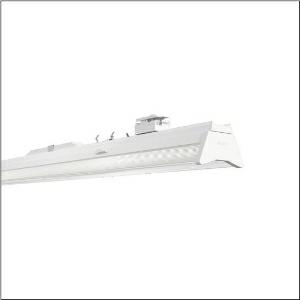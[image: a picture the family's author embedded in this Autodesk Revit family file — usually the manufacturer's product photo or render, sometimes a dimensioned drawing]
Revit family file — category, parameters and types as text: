
# Revit family: licross_11_performance_mo_51tm16mn4axg
name_source: partatom
category: Lighting Fixtures
units: mm (PartAtom-declared; Revit-internal decimal feet)

## family parameters
Cut with Voids When Loaded = No
Host = Face
Light Source = No
Part Type = Normal
Room Calculation Point = No
Round Connector Dimension = Use Diameter
Shared = No

## types (1)
- --- (1 x LED, 10160 lm, 55.3 W, 4000K)
    Apparent Load = 55 VA
    CIE Flux Codes = 66 88 96 79 100
    Color Rendering = 80
    Color Temperature = 4000K
    Default Elevation = 1800 mm
    Description = Licross 11 Performance MO, luminaire insert, of sheet steel, galvanised, coil coated, white, length: 1.500mm, width: 120mm, height: 123mm, LED rated luminous flux: 10.160lm, light colour: 840, SDCM (Standard Deviation of Colour Matching)MacAdam ≤ 2 SDCM (initial), control gear: ON/OFF Multilumen, with plug, 3-pole, with phase selection, mains connection: 220..240V, AC, 50/60Hz, rated input power: 55W, internal wiring halogen-free, primary light control with lens, of plastic, primary optical cover: cover, of PMMA, light emission: direct/indirect distribution, primary light characteristic: symmetric, protection rating (complete): IP40, insulation class (complete): insulation class I (protective earthing), certification: CE, ENEC, VDE, UKCA, protection symbol: D if used in an environment without relevant dust loads with corresponding accessories, impact resistance: IK06, permissible ambient temperature for indoor applications: -35..+40°C, corresponds to IFS (International Featured Standards) requirements for safety and quality in the food industry, reducing of maximum allowable ambient temperature of 5°C with ceiling mounting, LABS conformity tested according to VDMA 24364:2018-05, The light source and the operating device comply with the requirements of the Ecodesign Regulation (EU) 2019/2020 and are replaceable in accordance with this regulation, packaging unit: 1 piece
    Height = 114 mm
    Lamp = 1 x LED
    Lamp Light Flux = 10160 lm
    Lamp Power = 55.3 W
    Lamp count = 1
    Length = 1500 mm
    Luminous efficacy = 184 lm/W
    Manufacturer = Siteco
    ModVariant = No
    Model = 51TM16MN4AXG
    Mounting Place = Ceiling
    Mounting Type = Pendant
    Number of Poles = 1
    OnlyDefault = Yes
    Power Factor = 1
    Product Name = Licross 11 Performance MO
    Product group = luminaire insert | ceiling pendant
    ProductGroupID = 901
    Protection Class = Protection class I
    Protection Degree = IP 40
    RLX_Detail_Level = 1
    RLX_Emergency_Light_Flux = 0 lm
    RLX_Emergency_Type = 0
    RLX_Emergency_Type_DB = No
    RlxData = <blob elided: 32073 chars, md5=c2b481ec>
    Socket = socket
    Standby Power = 0 W
    System Light Flux = 10160 lm
    System Power = 55 W
    Type Comments = factory setting: luminous flux: 100 % | (A | C | E) | 126 mA
    Type Image = l_1256138.jpg
    URL = http://relux.com
    VarID = @adj_090575
    Voltage = 0 V
    Weight = 0.00 kg
    Width = 120 mm

## geometry (parser evidence)
native form markers: Blend x4, Sweep x13
no freeform markers — native parametric forms only
